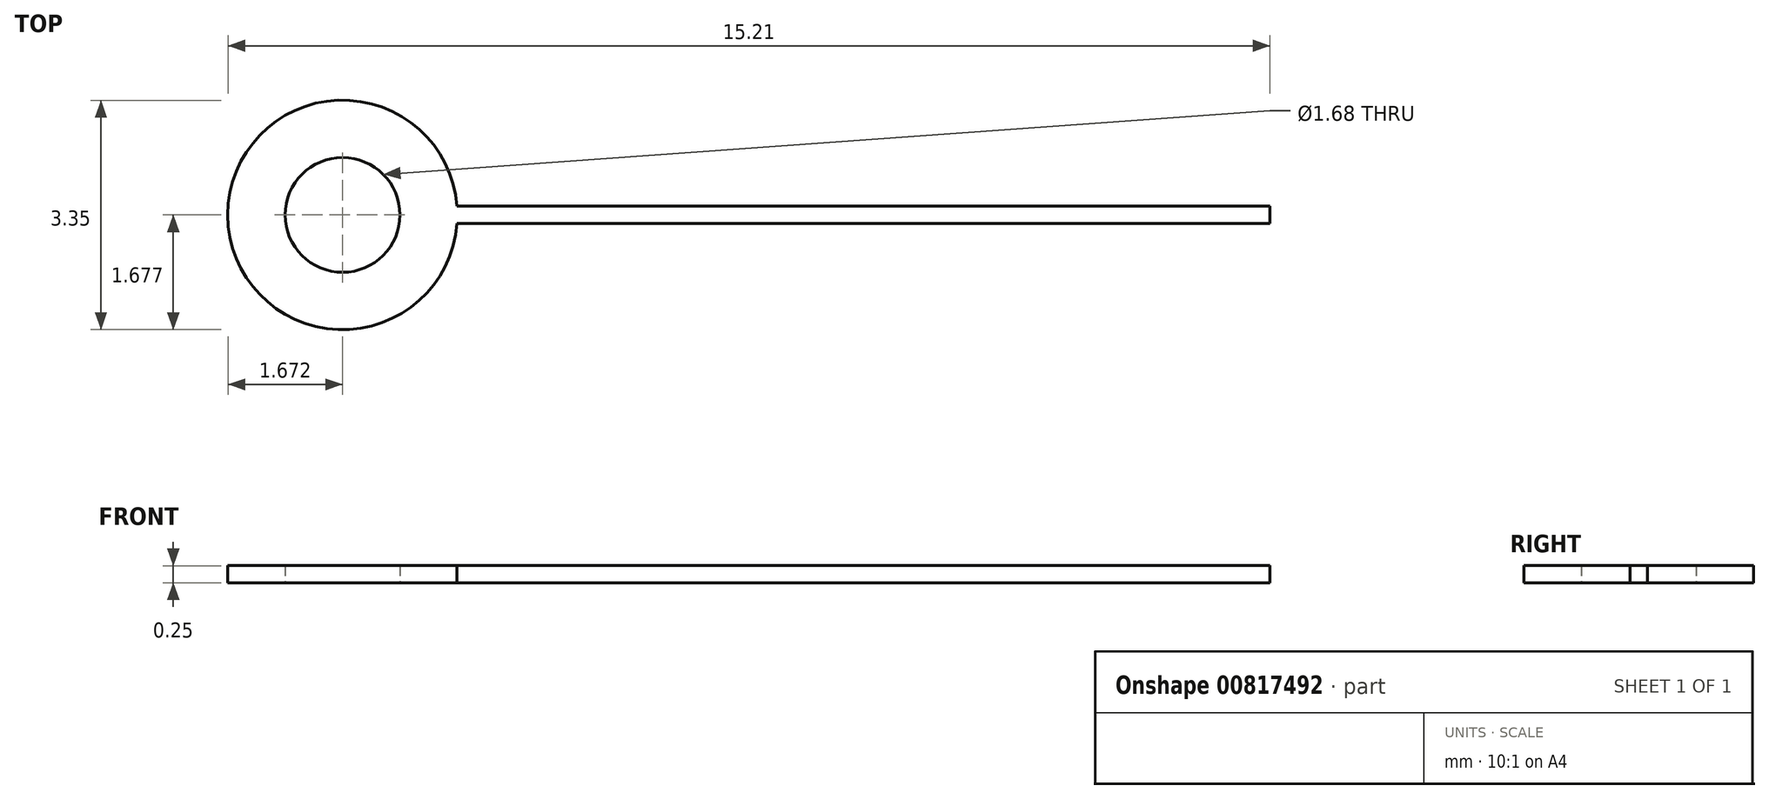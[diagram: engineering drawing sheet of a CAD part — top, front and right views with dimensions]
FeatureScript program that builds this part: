
annotation { "Feature Type Name" : "Feature", "Feature Type Description" : "" }
export const myFeature = defineFeature(function(context is Context, id is Id, definition is map)
    precondition{}
    {
        {
            var Q0;
            Q0=qCreatedBy(makeId("Top.planeOp"),FACE);
            var sketch = newSketch(context, id + "F0", { "sketchPlane" : qUnion([Q0])});
            skLineSegment(sketch, "E0.bottom", {"start": v(0, 0) * mm, "end": v(12.7, 0) * mm});
            skLineSegment(sketch, "E0.top", {"start": v(0, 0.25) * mm, "end": v(12.7, 0.25) * mm});
            skLineSegment(sketch, "E0.right", {"start": v(12.7, 0) * mm, "end": v(12.7, 0.25) * mm});
            skLineSegment(sketch, "E1", {"start": v(0, 0) * mm, "end": v(0, 0.25) * mm});
            skLineSegment(sketch, "E2", {"start": v(0, 0.13) * mm, "end": v(-0.84, 0.13) * mm});
            skLineSegment(sketch, "E3", {"start": v(0, 0.13) * mm, "end": v(0.84, 0.13) * mm});
            skCircle(sketch, "E4", {"center": v(-0.84, 0.13) * mm, "radius": 1.68 * mm});
            skCircle(sketch, "E5", {"center": v(-0.84, 0.13) * mm, "radius": 0.84 * mm});
            skSolve(sketch);
        }
        {
            var Q0;
            Q0 = qSketchRegion(id + "F0", true);
            extrude(context, id + "F1", {"entities" : qUnion([Q0]), "depth" : 0.25 * mm, "offsetDistance" : 25.4 * mm});
        }
    });
